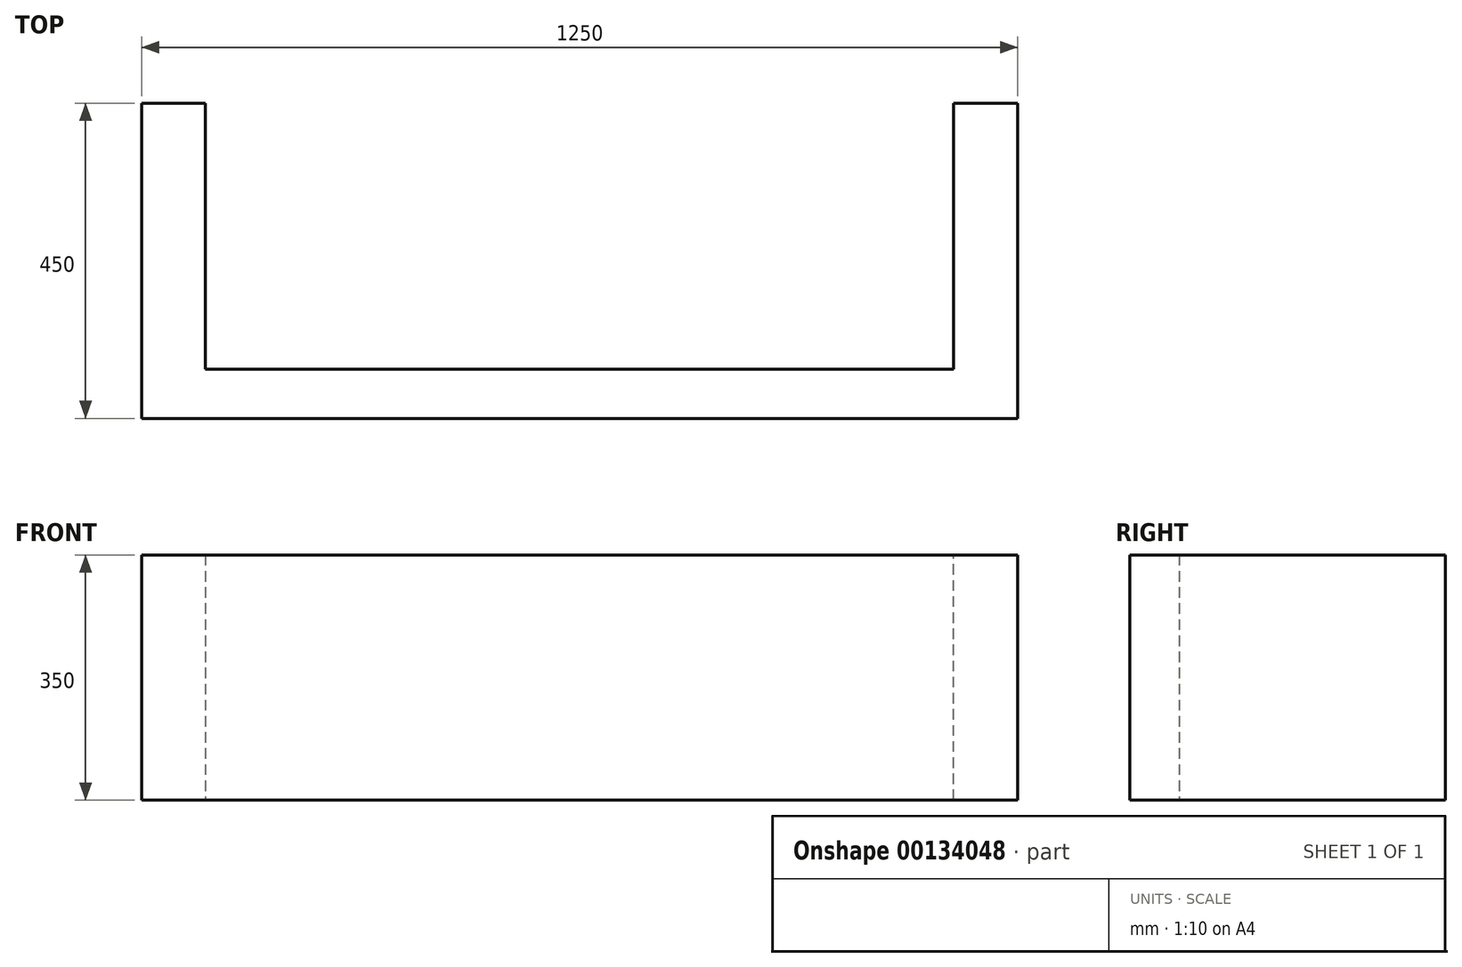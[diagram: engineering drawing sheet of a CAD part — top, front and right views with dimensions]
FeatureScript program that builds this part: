
annotation { "Feature Type Name" : "Feature", "Feature Type Description" : "" }
export const myFeature = defineFeature(function(context is Context, id is Id, definition is map)
    precondition{}
    {
        {
            var Q0;
            Q0=qCreatedBy(makeId("Front.planeOp"),FACE);
            var sketch = newSketch(context, id + "F0", { "sketchPlane" : qUnion([Q0])});
            skLineSegment(sketch, "E0.bottom", {"start": v(-1071.36, 181.66) * mm, "end": v(178.64, 181.66) * mm});
            skLineSegment(sketch, "E0.top", {"start": v(-1071.36, -168.34) * mm, "end": v(178.64, -168.34) * mm});
            skLineSegment(sketch, "E0.left", {"start": v(-1071.36, 181.66) * mm, "end": v(-1071.36, -168.34) * mm});
            skLineSegment(sketch, "E0.right", {"start": v(178.64, 181.66) * mm, "end": v(178.64, -168.34) * mm});
            skSolve(sketch);
        }
        {
            var Q0;
            Q0=makeQuery(id+"F0.imprint","IMPRINT",FACE,{"disambiguationData":[TD([[makeQuery(id+"F0.imprint","IMPRINT",EDGE,{"derivedFrom":sQuery(id+"F0.wireOp",EDGE,"E0.bottom")}),-1.0]])]});
            extrude(context, id + "F1", {"entities" : qUnion([Q0]), "depth" : 70 * mm});
        }
        {
            var Q0;
            Q0=makeQuery(id+"F1.opExtrude","CAP_FACE",FACE,{"disambiguationData":[OSD([sQuery(id+"F0.wireOp",EDGE,"E0.bottom"),sQuery(id+"F0.wireOp",EDGE,"E0.top"),sQuery(id+"F0.wireOp",EDGE,"E0.left"),sQuery(id+"F0.wireOp",EDGE,"E0.right")])],"isStart":true});
            var sketch = newSketch(context, id + "F2", { "sketchPlane" : qUnion([Q0])});
            skLineSegment(sketch, "E1.bottom", {"start": v(-178.64, -168.34) * mm, "end": v(-86.93, -168.34) * mm});
            skLineSegment(sketch, "E1.top", {"start": v(-178.64, 181.66) * mm, "end": v(-86.93, 181.66) * mm});
            skLineSegment(sketch, "E1.left", {"start": v(-178.64, -168.34) * mm, "end": v(-178.64, 181.66) * mm});
            skLineSegment(sketch, "E1.right", {"start": v(-86.93, -168.34) * mm, "end": v(-86.93, 181.66) * mm});
            skLineSegment(sketch, "E2.bottom", {"start": v(1071.36, 181.66) * mm, "end": v(980.72, 181.66) * mm});
            skLineSegment(sketch, "E2.top", {"start": v(1071.36, -168.34) * mm, "end": v(980.72, -168.34) * mm});
            skLineSegment(sketch, "E2.left", {"start": v(1071.36, 181.66) * mm, "end": v(1071.36, -168.34) * mm});
            skLineSegment(sketch, "E2.right", {"start": v(980.72, 181.66) * mm, "end": v(980.72, -168.34) * mm});
            skSolve(sketch);
        }
        {
            var Q0;
            Q0=makeQuery(id+"F2.imprint","IMPRINT",FACE,{"disambiguationData":[TD([[makeQuery(id+"F2.imprint","IMPRINT",EDGE,{"derivedFrom":sQuery(id+"F2.wireOp",EDGE,"E1.bottom")}),-1.0]])]});
            var Q1;
            Q1=makeQuery(id+"F2.imprint","IMPRINT",FACE,{"disambiguationData":[TD([[makeQuery(id+"F2.imprint","IMPRINT",EDGE,{"derivedFrom":sQuery(id+"F2.wireOp",EDGE,"E2.bottom")}),1.0]])]});
            extrude(context, id + "F3", {"entities" : qUnion([Q0, Q1]), "operationType" : NewBodyOperationType.ADD, "depth" : 380 * mm});
        }
    });
